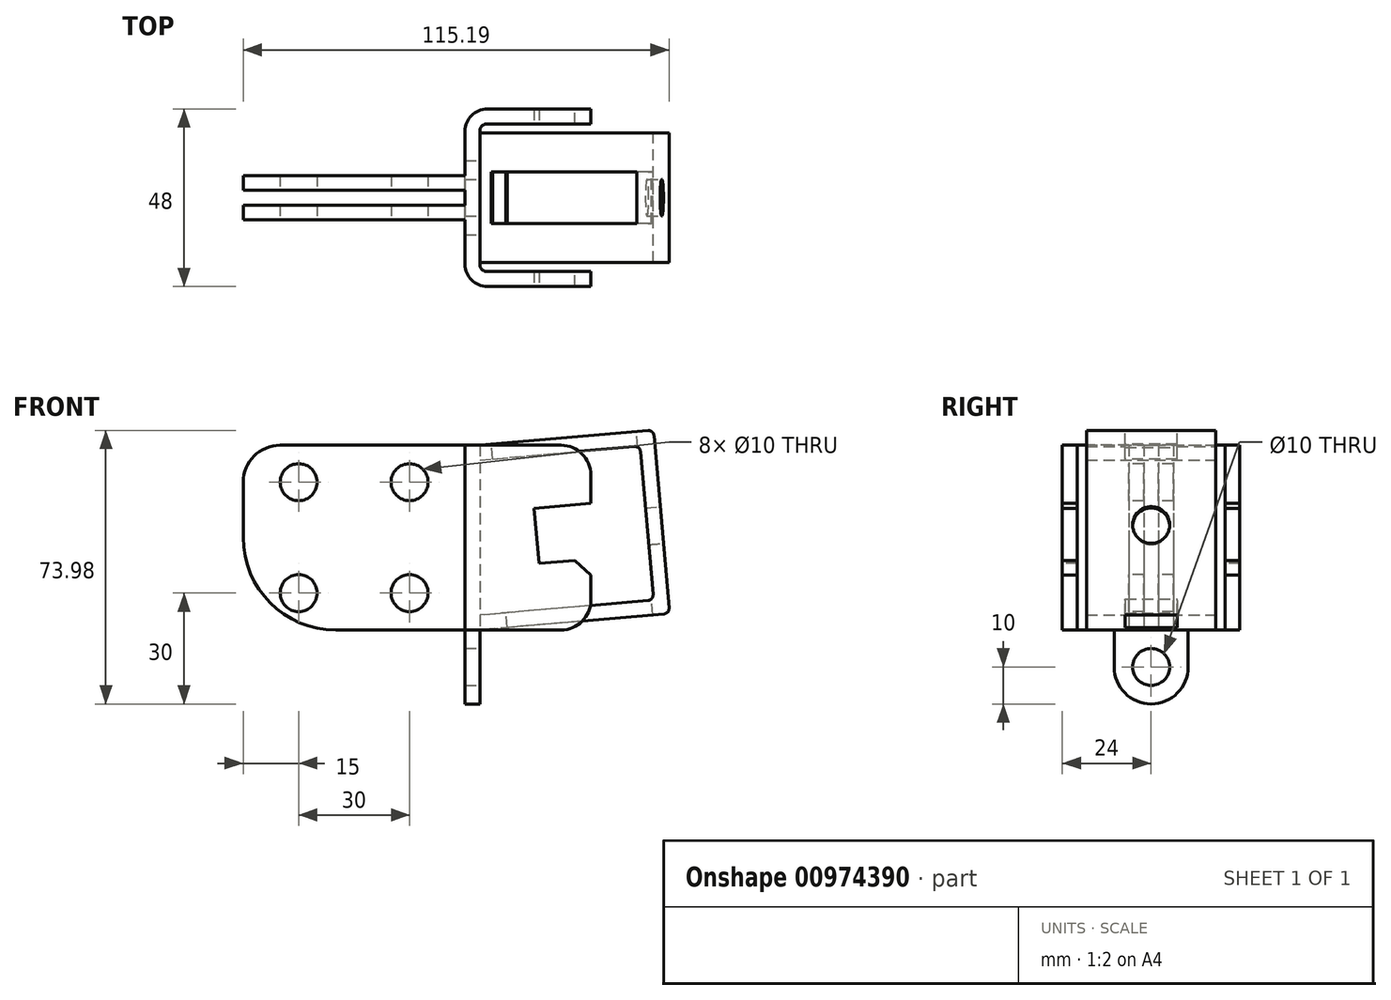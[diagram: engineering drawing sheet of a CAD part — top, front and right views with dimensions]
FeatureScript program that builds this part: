
annotation { "Feature Type Name" : "Feature", "Feature Type Description" : "" }
export const myFeature = defineFeature(function(context is Context, id is Id, definition is map)
    precondition{}
    {
        {
            assignVariable(context, id + "F0", {"name" : "PlatLargeur", "anyValue" : 50});
        }
        {
            var Q0;
            Q0=qCreatedBy(makeId("Top.planeOp"),FACE);
            var sketch = newSketch(context, id + "F1", { "sketchPlane" : qUnion([Q0])});
            skLineSegment(sketch, "E0", {"start": v(-57.64, 0) * mm, "end": v(53.74, 0) * mm, "construction": true});
            skLineSegment(sketch, "E1", {"start": v(0, 0) * mm, "end": v(0, -18) * mm});
            skLineSegment(sketch, "E2", {"start": v(-4, -2) * mm, "end": v(-64, -2) * mm});
            skLineSegment(sketch, "E3", {"start": v(2, -20) * mm, "end": v(30, -20) * mm});
            skLineSegment(sketch, "E4.MirrorCS", {"start": v(2, 20) * mm, "end": v(30, 20) * mm});
            skLineSegment(sketch, "E5.MirrorCS", {"start": v(0, 0) * mm, "end": v(0, 18) * mm});
            skLineSegment(sketch, "E6.MirrorCS", {"start": v(-4, 2) * mm, "end": v(-64, 2) * mm});
            skPoint(sketch, "E7.visualSharp", {"position": v(0, 20) * mm});
            skArc(sketch, "E7.filletArc", {"start": v(2, 20) * mm, "mid": v(0.59, 19.41) * mm, "end": v(0, 18) * mm});
            skPoint(sketch, "E8.visualSharp", {"position": v(0, -20) * mm});
            skArc(sketch, "E8.filletArc", {"start": v(0, -18) * mm, "mid": v(0.59, -19.41) * mm, "end": v(2, -20) * mm});
            skLineSegment(sketch, "E9.0", {"start": v(2, 24) * mm, "end": v(30, 24) * mm});
            skArc(sketch, "E9.1", {"start": v(2, 24) * mm, "mid": v(-2.24, 22.24) * mm, "end": v(-4, 18) * mm});
            skLineSegment(sketch, "E9.2", {"start": v(2, -24) * mm, "end": v(30, -24) * mm});
            skArc(sketch, "E9.3", {"start": v(-4, -18) * mm, "mid": v(-2.24, -22.24) * mm, "end": v(2, -24) * mm});
            skLineSegment(sketch, "E9.4", {"start": v(-4, 0) * mm, "end": v(-4, -18) * mm});
            skLineSegment(sketch, "E9.5", {"start": v(-4, 0) * mm, "end": v(-4, 18) * mm});
            skLineSegment(sketch, "E10", {"start": v(30, 24) * mm, "end": v(30, 20) * mm});
            skLineSegment(sketch, "E11", {"start": v(30, -20) * mm, "end": v(30, -24) * mm});
            skLineSegment(sketch, "E12.0", {"start": v(-4, 6) * mm, "end": v(-64, 6) * mm});
            skLineSegment(sketch, "E13.MirrorCS", {"start": v(-4, -6) * mm, "end": v(-64, -6) * mm});
            skLineSegment(sketch, "E14", {"start": v(-64, 6) * mm, "end": v(-64, 2) * mm});
            skLineSegment(sketch, "E15", {"start": v(-64, -2) * mm, "end": v(-64, -6) * mm});
            skSolve(sketch);
        }
        {
            var Q0;
            Q0 = qSketchRegion(id + "F1", true);
            extrude(context, id + "F2", {"entities" : qUnion([Q0]), "depth" : (getVariable(context, 'PlatLargeur')) * mm, "offsetDistance" : 25 * mm});
        }
        {
            var Q0;
            Q0=makeQuery(id+"F2.opExtrude","CAP_EDGE",EDGE,{"disambiguationData":[OSD([sQuery(id+"F1.wireOp",EDGE,"E15")])],"isStart":false});
            var Q1;
            Q1=makeQuery(id+"F2.opExtrude","CAP_EDGE",EDGE,{"disambiguationData":[OSD([sQuery(id+"F1.wireOp",EDGE,"E14")])],"isStart":false});
            fillet(context, id + "F3", {"entities" : qUnion([Q0, Q1]), "radius" : 10 * mm, "tangentPropagation" : true, "allowEdgeOverflow" : false});
        }
        {
            var Q0;
            Q0=makeQuery(id+"F2.opExtrude","CAP_EDGE",EDGE,{"disambiguationData":[OSD([sQuery(id+"F1.wireOp",EDGE,"E14")])],"isStart":true});
            var Q1;
            Q1=makeQuery(id+"F2.opExtrude","CAP_EDGE",EDGE,{"disambiguationData":[OSD([sQuery(id+"F1.wireOp",EDGE,"E15")])],"isStart":true});
            fillet(context, id + "F4", {"entities" : qUnion([Q0, Q1]), "radius" : 25 * mm, "tangentPropagation" : true, "allowEdgeOverflow" : false});
        }
        {
            var Q0;
            Q0=makeQuery(id+"F2.opExtrude","SWEPT_FACE",FACE,{"disambiguationData":[OSD([sQuery(id+"F1.wireOp",EDGE,"E13.MirrorCS")])]});
            var sketch = newSketch(context, id + "F5", { "sketchPlane" : qUnion([Q0])});
            skLineSegment(sketch, "E16", {"start": v(-7.89, 40) * mm, "end": v(-50.15, 40) * mm, "construction": true});
            skLineSegment(sketch, "E17", {"start": v(-7.5, 10) * mm, "end": v(-50.44, 10) * mm, "construction": true});
            skLineSegment(sketch, "E18", {"start": v(-49, 45.5) * mm, "end": v(-49, 10.29) * mm, "construction": true});
            skLineSegment(sketch, "E19", {"start": v(-19, 45.12) * mm, "end": v(-19, 5.23) * mm, "construction": true});
            skCircle(sketch, "E20", {"center": v(-49, 40) * mm, "radius": 5 * mm});
            skCircle(sketch, "E21", {"center": v(-19, 40) * mm, "radius": 5 * mm});
            skCircle(sketch, "E22", {"center": v(-19, 10) * mm, "radius": 5 * mm});
            skCircle(sketch, "E23", {"center": v(-49, 10) * mm, "radius": 5 * mm});
            skSolve(sketch);
        }
        {
            var Q0;
            Q0 = qSketchRegion(id + "F5", true);
            extrude(context, id + "F6", {"entities" : qUnion([Q0]), "operationType" : NewBodyOperationType.REMOVE, "endBound" : BoundingType.THROUGH_ALL, "oppositeDirection" : true, "depth" : 25 * mm, "offsetDistance" : 25 * mm});
        }
        {
            var Q0;
            Q0=makeQuery(id+"F2.opExtrude","SWEPT_FACE",FACE,{"disambiguationData":[OSD([sQuery(id+"F1.wireOp",EDGE,"E9.2")])]});
            var sketch = newSketch(context, id + "F7", { "sketchPlane" : qUnion([Q0])});
            skLineSegment(sketch, "E24.bottom", {"start": v(14.7, 32.94) * mm, "end": v(30, 34.28) * mm});
            skLineSegment(sketch, "E24.top", {"start": v(16, 18) * mm, "end": v(31.3, 19.34) * mm});
            skLineSegment(sketch, "E24.left", {"start": v(14.7, 32.94) * mm, "end": v(16, 18) * mm});
            skLineSegment(sketch, "E24.right", {"start": v(30, 34.28) * mm, "end": v(31.3, 19.34) * mm});
            skSolve(sketch);
        }
        {
            var Q0;
            {var subQ0=sQuery(id+"F7.wireOp",EDGE,"E24.bottom");Q0=makeQuery(id+"F7.imprint","IMPRINT",FACE,{"disambiguationData":[TD([[makeQuery(id+"F7.imprint","IMPRINT",EDGE,{"derivedFrom":subQ0}),-1.0]])]});}
            extrude(context, id + "F8", {"entities" : qUnion([Q0]), "operationType" : NewBodyOperationType.REMOVE, "endBound" : BoundingType.THROUGH_ALL, "oppositeDirection" : true, "depth" : 25 * mm, "offsetDistance" : 25 * mm});
        }
        {
            var Q0;
            {var subQ0=sQuery(id+"F1.wireOp",EDGE,"E11");var subQ1=sQuery(id+"F7.wireOp",EDGE,"E24.bottom");Q0=makeQuery(id+"F8.boolean.opBoolean","COPY",EDGE,{"disambiguationData":[topologyDisambiguationEdgeConnected([makeQuery(id+"F2.opExtrude","SWEPT_FACE",FACE,{"disambiguationData":[OSD([subQ0])]})])],"derivedFrom":makeQuery(id+"F8.opExtrude","SWEPT_EDGE",EDGE,{"disambiguationData":[OSD([sQuery(id+"F1.wireOp",EDGE,"E9.2"),subQ0,subQ1,sQuery(id+"F7.wireOp",EDGE,"E24.right")])]})});}
            var Q1;
            {var subQ0=sQuery(id+"F7.wireOp",EDGE,"E24.bottom");Q1=makeQuery(id+"F8.boolean.opBoolean","COPY",EDGE,{"disambiguationData":[topologyDisambiguationEdgeConnected([makeQuery(id+"F2.opExtrude","SWEPT_FACE",FACE,{"disambiguationData":[OSD([sQuery(id+"F1.wireOp",EDGE,"E10")])]})])],"derivedFrom":makeQuery(id+"F8.opExtrude","SWEPT_EDGE",EDGE,{"disambiguationData":[OSD([sQuery(id+"F1.wireOp",EDGE,"E9.2"),sQuery(id+"F1.wireOp",EDGE,"E11"),subQ0,sQuery(id+"F7.wireOp",EDGE,"E24.right")])]})});}
            var Q2;
            {var subQ0=sQuery(id+"F7.wireOp",EDGE,"E24.top");Q2=makeQuery(id+"F8.boolean.opBoolean","COPY",EDGE,{"disambiguationData":[topologyDisambiguationEdgeConnected([makeQuery(id+"F2.opExtrude","SWEPT_FACE",FACE,{"disambiguationData":[OSD([sQuery(id+"F1.wireOp",EDGE,"E10")])]})])],"derivedFrom":makeQuery(id+"F8.opExtrude","SWEPT_EDGE",EDGE,{"disambiguationData":[OSD([sQuery(id+"F1.wireOp",EDGE,"E9.2"),sQuery(id+"F1.wireOp",EDGE,"E11"),subQ0])]})});}
            var Q3;
            {var subQ0=sQuery(id+"F1.wireOp",EDGE,"E11");var subQ1=sQuery(id+"F7.wireOp",EDGE,"E24.top");Q3=makeQuery(id+"F8.boolean.opBoolean","COPY",EDGE,{"disambiguationData":[topologyDisambiguationEdgeConnected([makeQuery(id+"F2.opExtrude","SWEPT_FACE",FACE,{"disambiguationData":[OSD([subQ0])]})])],"derivedFrom":makeQuery(id+"F8.opExtrude","SWEPT_EDGE",EDGE,{"disambiguationData":[OSD([sQuery(id+"F1.wireOp",EDGE,"E9.2"),subQ0,subQ1])]})});}
            chamfer(context, id + "F9", {"entities" : qUnion([Q0, Q1, Q2, Q3]), "width" : 4 * mm, "tangentPropagation" : true});
        }
        {
            var Q0;
            Q0=makeQuery(id+"F2.opExtrude","CAP_EDGE",EDGE,{"disambiguationData":[OSD([sQuery(id+"F1.wireOp",EDGE,"E11")])],"isStart":false});
            var Q1;
            Q1=makeQuery(id+"F2.opExtrude","CAP_EDGE",EDGE,{"disambiguationData":[OSD([sQuery(id+"F1.wireOp",EDGE,"E10")])],"isStart":false});
            var Q2;
            Q2=makeQuery(id+"F2.opExtrude","CAP_EDGE",EDGE,{"disambiguationData":[OSD([sQuery(id+"F1.wireOp",EDGE,"E10")])],"isStart":true});
            var Q3;
            Q3=makeQuery(id+"F2.opExtrude","CAP_EDGE",EDGE,{"disambiguationData":[OSD([sQuery(id+"F1.wireOp",EDGE,"E11")])],"isStart":true});
            fillet(context, id + "F10", {"entities" : qUnion([Q0, Q1, Q2, Q3]), "radius" : 8 * mm, "tangentPropagation" : true, "allowEdgeOverflow" : false});
        }
        {
            var Q0;
            Q0=makeQuery(id+"F2.opExtrude","SWEPT_FACE",FACE,{"disambiguationData":[OSD([sQuery(id+"F1.wireOp",EDGE,"E1"),sQuery(id+"F1.wireOp",EDGE,"E5.MirrorCS")])]});
            var sketch = newSketch(context, id + "F11", { "sketchPlane" : qUnion([Q0])});
            skLineSegment(sketch, "E25", {"start": v(0, 0) * mm, "end": v(0, -12.85) * mm, "construction": true});
            skLineSegment(sketch, "E26", {"start": v(-10, 0) * mm, "end": v(-10, -10) * mm});
            skLineSegment(sketch, "E27.MirrorCS", {"start": v(10, 0) * mm, "end": v(10, -10) * mm});
            skArc(sketch, "E28", {"start": v(-10, -10) * mm, "mid": v(0, -20) * mm, "end": v(10, -10) * mm});
            skCircle(sketch, "E29", {"center": v(0, -10) * mm, "radius": 5 * mm});
            skSolve(sketch);
        }
        {
            var Q0;
            {var subQ1=sQuery(id+"F11.wireOp",EDGE,"E26");Q0=makeQuery(id+"F11.imprint","IMPRINT",FACE,{"disambiguationData":[TD([[makeQuery(id+"F11.imprint","IMPRINT",EDGE,{"derivedFrom":subQ1}),1.0]])]});}
            var Q1;
            Q1=makeQuery(id+"F2.opExtrude","SWEPT_FACE",FACE,{"disambiguationData":[OSD([sQuery(id+"F1.wireOp",EDGE,"E9.4")])]});
            extrude(context, id + "F12", {"entities" : qUnion([Q0]), "operationType" : NewBodyOperationType.ADD, "endBound" : BoundingType.UP_TO_SURFACE, "oppositeDirection" : true, "depth" : 25 * mm, "endBoundEntityFace" : qUnion([Q1]), "offsetDistance" : 25 * mm});
        }
        {
            var Q0;
            Q0=qCreatedBy(makeId("Front.planeOp"),FACE);
            var sketch = newSketch(context, id + "F13", { "sketchPlane" : qUnion([Q0])});
            skPoint(sketch, "E30.0", {"position": v(0, 50) * mm});
            skPoint(sketch, "E31.0", {"position": v(0, 0) * mm});
            skLineSegment(sketch, "E32", {"start": v(0, 50) * mm, "end": v(45.48, 53.98) * mm});
            skLineSegment(sketch, "E33", {"start": v(47.1, 52.62) * mm, "end": v(51.18, 5.98) * mm});
            skLineSegment(sketch, "E34", {"start": v(49.82, 4.36) * mm, "end": v(0, 0) * mm});
            skLineSegment(sketch, "E35.0", {"start": v(45.48, 8) * mm, "end": v(0, 4.02) * mm});
            skLineSegment(sketch, "E35.1", {"start": v(43.47, 48.28) * mm, "end": v(46.85, 9.62) * mm});
            skLineSegment(sketch, "E35.2", {"start": v(0, 45.98) * mm, "end": v(41.84, 49.65) * mm});
            skPoint(sketch, "E36.visualSharp", {"position": v(43.33, 49.78) * mm});
            skArc(sketch, "E36.filletArc", {"start": v(43.47, 48.28) * mm, "mid": v(42.94, 49.3) * mm, "end": v(41.84, 49.65) * mm});
            skPoint(sketch, "E37.visualSharp", {"position": v(46.98, 8.13) * mm});
            skArc(sketch, "E37.filletArc", {"start": v(45.48, 8) * mm, "mid": v(46.5, 8.52) * mm, "end": v(46.85, 9.62) * mm});
            skPoint(sketch, "E38.visualSharp", {"position": v(46.97, 54.1) * mm});
            skArc(sketch, "E38.filletArc", {"start": v(47.1, 52.62) * mm, "mid": v(46.57, 53.63) * mm, "end": v(45.48, 53.98) * mm});
            skPoint(sketch, "E39.visualSharp", {"position": v(51.31, 4.49) * mm});
            skArc(sketch, "E39.filletArc", {"start": v(49.82, 4.36) * mm, "mid": v(50.84, 4.89) * mm, "end": v(51.18, 5.98) * mm});
            skLineSegment(sketch, "E40", {"start": v(0, 50) * mm, "end": v(0, 45.98) * mm});
            skLineSegment(sketch, "E41", {"start": v(0, 4.02) * mm, "end": v(0, 0) * mm});
            skSolve(sketch);
        }
        {
            var Q0;
            Q0 = qSketchRegion(id + "F13", true);
            extrude(context, id + "F14", {"entities" : qUnion([Q0]), "operationType" : NewBodyOperationType.ADD, "endBound" : BoundingType.SYMMETRIC, "depth" : 35 * mm, "offsetDistance" : 25 * mm});
        }
        {
            var Q0;
            Q0=makeQuery(id+"F14.opExtrude","SWEPT_FACE",FACE,{"disambiguationData":[OSD([sQuery(id+"F13.wireOp",EDGE,"E32")])]});
            var sketch = newSketch(context, id + "F15", { "sketchPlane" : qUnion([Q0])});
            skLineSegment(sketch, "E42", {"start": v(50, 0) * mm, "end": v(4.36, 0) * mm, "construction": true});
            skLineSegment(sketch, "E43.bottom", {"start": v(7.45, 7.03) * mm, "end": v(46.92, 7.03) * mm});
            skLineSegment(sketch, "E43.top", {"start": v(7.45, -7.03) * mm, "end": v(46.92, -7.03) * mm});
            skLineSegment(sketch, "E43.left", {"start": v(7.45, 7.03) * mm, "end": v(7.45, -7.03) * mm});
            skLineSegment(sketch, "E43.right", {"start": v(46.92, 7.03) * mm, "end": v(46.92, -7.03) * mm});
            skPoint(sketch, "E43.middle", {"position": v(27.18, 0) * mm});
            skSolve(sketch);
        }
        {
            var Q0;
            Q0 = qSketchRegion(id + "F15", true);
            extrude(context, id + "F16", {"entities" : qUnion([Q0]), "operationType" : NewBodyOperationType.REMOVE, "endBound" : BoundingType.THROUGH_ALL, "oppositeDirection" : true, "depth" : 25 * mm, "offsetDistance" : 25 * mm});
        }
        {
            var Q0;
            Q0=makeQuery(id+"F14.opExtrude","SWEPT_FACE",FACE,{"disambiguationData":[OSD([sQuery(id+"F13.wireOp",EDGE,"E33")])]});
            var sketch = newSketch(context, id + "F17", { "sketchPlane" : qUnion([Q0])});
            skLineSegment(sketch, "E44", {"start": v(0, 1.5) * mm, "end": v(0, 48.3) * mm, "construction": true});
            skLineSegment(sketch, "E45.0", {"start": v(-24, 31.54) * mm, "end": v(-24, 16.54) * mm, "construction": true});
            skLineSegment(sketch, "E46.0", {"start": v(24, 16.54) * mm, "end": v(24, 31.54) * mm, "construction": true});
            skLineSegment(sketch, "E47", {"start": v(24, 24.04) * mm, "end": v(-24, 24.04) * mm, "construction": true});
            skCircle(sketch, "E48", {"center": v(0, 24.04) * mm, "radius": 5 * mm});
            skSolve(sketch);
        }
        {
            var Q0;
            Q0 = qSketchRegion(id + "F17", true);
            extrude(context, id + "F18", {"entities" : qUnion([Q0]), "operationType" : NewBodyOperationType.REMOVE, "endBound" : BoundingType.UP_TO_NEXT, "oppositeDirection" : true, "depth" : 25 * mm, "offsetDistance" : 25 * mm});
        }
    });
